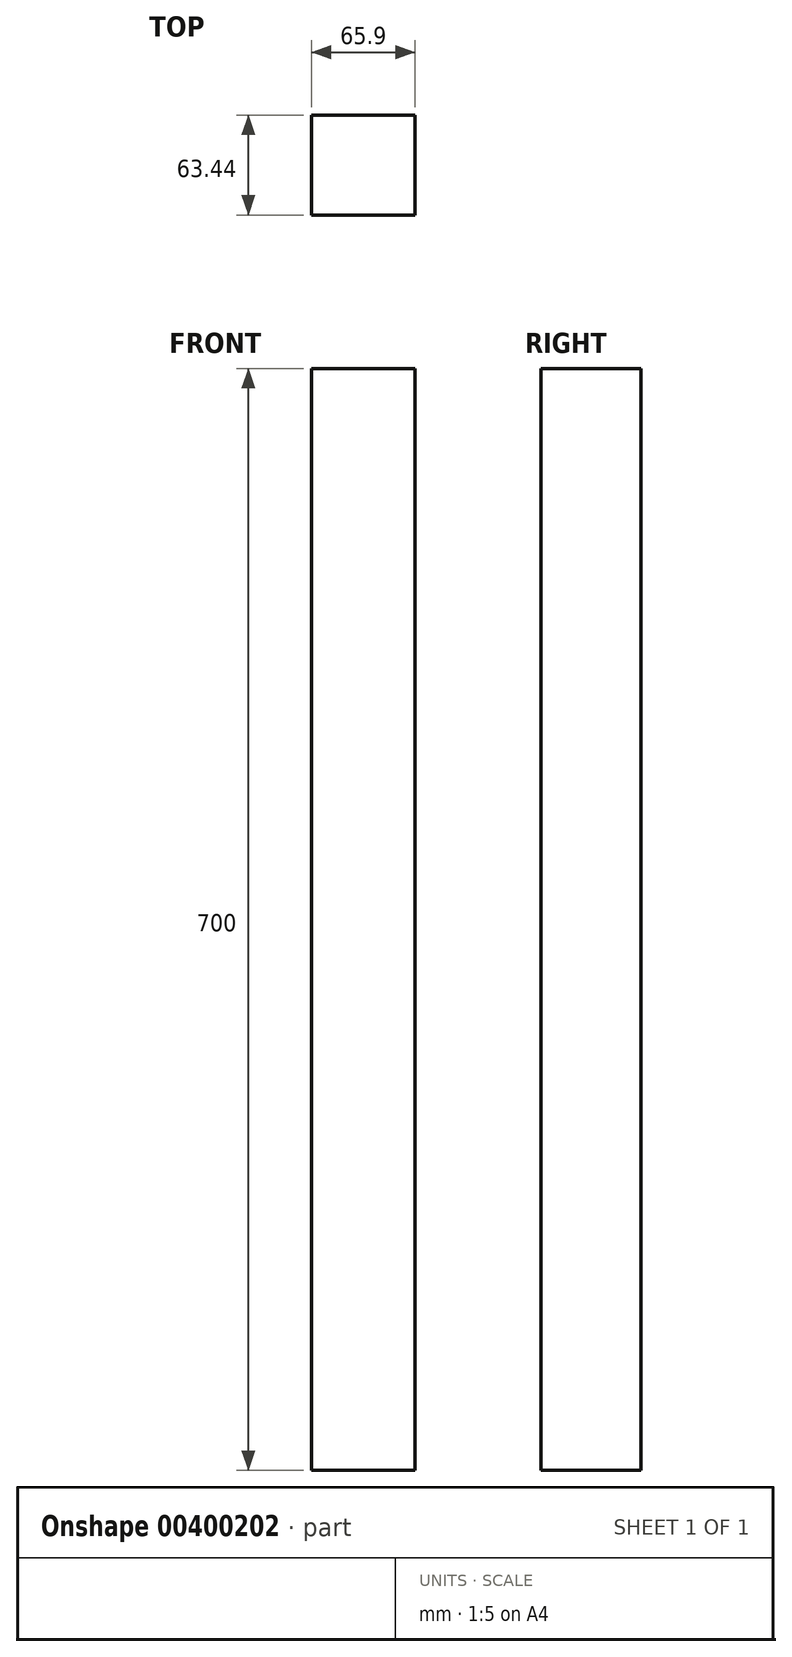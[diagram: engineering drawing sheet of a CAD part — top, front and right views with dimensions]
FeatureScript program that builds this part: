
annotation { "Feature Type Name" : "Feature", "Feature Type Description" : "" }
export const myFeature = defineFeature(function(context is Context, id is Id, definition is map)
    precondition{}
    {
        {
            var Q0;
            Q0=qCreatedBy(makeId("Top.planeOp"),FACE);
            var sketch = newSketch(context, id + "F0", { "sketchPlane" : qUnion([Q0])});
            skLineSegment(sketch, "E0.bottom", {"start": v(0, 0) * mm, "end": v(65.9, 0) * mm});
            skLineSegment(sketch, "E0.top", {"start": v(0, 63.44) * mm, "end": v(65.9, 63.44) * mm});
            skLineSegment(sketch, "E0.left", {"start": v(0, 0) * mm, "end": v(0, 63.44) * mm});
            skLineSegment(sketch, "E0.right", {"start": v(65.9, 0) * mm, "end": v(65.9, 63.44) * mm});
            skSolve(sketch);
        }
        {
            var Q0;
            Q0=makeQuery(id+"F0.imprint","IMPRINT",FACE,{"disambiguationData":[TD([[makeQuery(id+"F0.imprint","IMPRINT",EDGE,{"derivedFrom":sQuery(id+"F0.wireOp",EDGE,"E0.bottom")}),1.0]])]});
            extrude(context, id + "F1", {"entities" : qUnion([Q0]), "depth" : 700 * mm});
        }
    });
